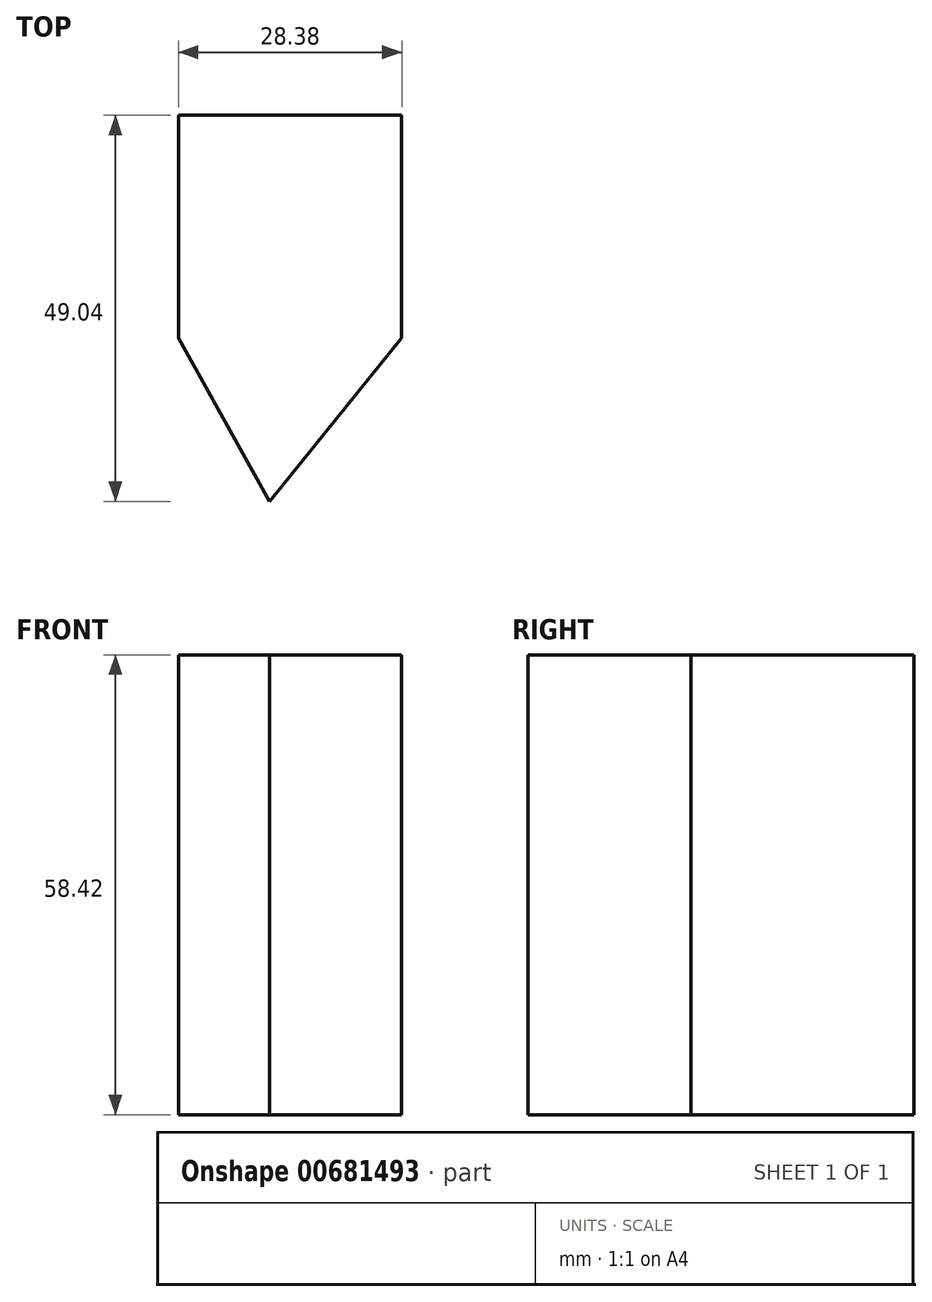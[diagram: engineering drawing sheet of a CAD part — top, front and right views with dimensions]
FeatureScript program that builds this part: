
annotation { "Feature Type Name" : "Feature", "Feature Type Description" : "" }
export const myFeature = defineFeature(function(context is Context, id is Id, definition is map)
    precondition{}
    {
        {
            var Q0;
            Q0=qCreatedBy(makeId("Top.planeOp"),FACE);
            var sketch = newSketch(context, id + "F0", { "sketchPlane" : qUnion([Q0])});
            skLineSegment(sketch, "E0", {"start": v(0, 0) * mm, "end": v(0, 28.3) * mm});
            skLineSegment(sketch, "E1", {"start": v(0, 28.3) * mm, "end": v(28.38, 28.3) * mm});
            skLineSegment(sketch, "E2", {"start": v(28.38, 28.3) * mm, "end": v(28.38, 0) * mm});
            skLineSegment(sketch, "E3", {"start": v(28.38, 0) * mm, "end": v(11.58, -20.73) * mm});
            skLineSegment(sketch, "E4", {"start": v(11.58, -20.73) * mm, "end": v(0, 0) * mm});
            skSolve(sketch);
        }
        {
            var Q0;
            Q0 = qSketchRegion(id + "F0", true);
            extrude(context, id + "F1", {"entities" : qUnion([Q0]), "depth" : 58.42 * mm, "offsetDistance" : 25.4 * mm});
        }
    });
